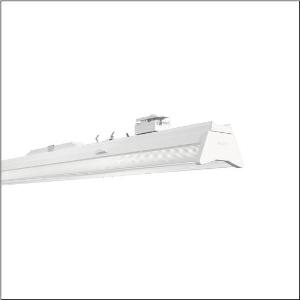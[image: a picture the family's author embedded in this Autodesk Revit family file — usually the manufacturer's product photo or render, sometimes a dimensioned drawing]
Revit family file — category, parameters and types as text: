
# Revit family: licross_r__11_performance_tw_51td16tnt85x_7c56
name_source: partatom
category: Lighting Fixtures
units: mm (PartAtom-declared; Revit-internal decimal feet)

## family parameters
Cut with Voids When Loaded = No
Host = Face
Light Source = No
Part Type = Normal
Room Calculation Point = No
Round Connector Dimension = Use Diameter
Shared = No

## types (1)
- --- (1 x LED 2700 K ... 6500 K, 8930 lm, 56 W, 2700K)
    Apparent Load = 56 VA
    CIE Flux Codes = 63 87 95 78 100
    Color Rendering = 80
    Color Temperature = 2700K
    Default Elevation = 1800 mm
    Description = Licross® 11 Performance TW, luminaire insert, of sheet steel, galvanised, coil coated, white, length: 1.500mm, width: 120mm, height: 123mm, LED rated luminous flux: 8.930lm, light colour: 8tw, control gear: DALI DT8, with plug, 5-pole, with phase selection, mains connection: 220..240V, AC, 50/60Hz, rated input power: 56W, halogen-free wiring, primary light control with lens, of plastic, primary optical cover: cover, of PMMA, light emission: direct/indirect distribution, primary light characteristic: symmetric, protection rating (complete): IP54, insulation class (complete): insulation class I (protective earthing), certification: CE, ENEC, VDE, UKCA, protection symbol: D if used in an environment with non-conductive dust loads with corresponding accessories, impact resistance: IK06, permissible ambient temperature for indoor applications: -25..+35°C, corresponds to IFS (International Featured Standards) requirements for safety and quality in the food industry, reducing of maximum allowable ambient temperature of 5°C with ceiling mounting, LABS conformity tested according to VDMA 24364:2018-05, packaging unit: 1 piece
    Height = 114 mm
    Lamp = 1 x LED 2700 K ... 6500 K
    Lamp Light Flux = 8930 lm
    Lamp Power = 56 W
    Lamp count = 1
    Length = 1500 mm
    Luminous efficacy = 159 lm/W
    Manufacturer = Siteco
    ModVariant = No
    Model = 51TD16TNT85X
    Mounting Place = Ceiling
    Mounting Type = Pendant
    Number of Poles = 1
    OnlyDefault = Yes
    Power Factor = 1
    Product Name = Licross® 11 Performance TW
    Product group = luminaire insert
    ProductGroupID = 901
    Protection Class = Protection class I
    Protection Degree = IP 54
    RLX_Detail_Level = 1
    RLX_Emergency_Light_Flux = 0 lm
    RLX_Emergency_Type = 0
    RLX_Emergency_Type_DB = No
    RlxData = <blob elided: 30337 chars, md5=e333f244>
    Socket = socket
    Standby Power = 0 W
    System Light Flux = 8930 lm
    System Power = 56 W
    Type Comments = individual setting: CCT=2700K
    Type Image = l_1256138.jpg
    URL = http://relux.com
    VarID = @adj_016023
    Voltage = 0 V
    Weight = 0.00 kg
    Width = 120 mm

## geometry (parser evidence)
native form markers: Blend x4, Sweep x14
no freeform markers — native parametric forms only
